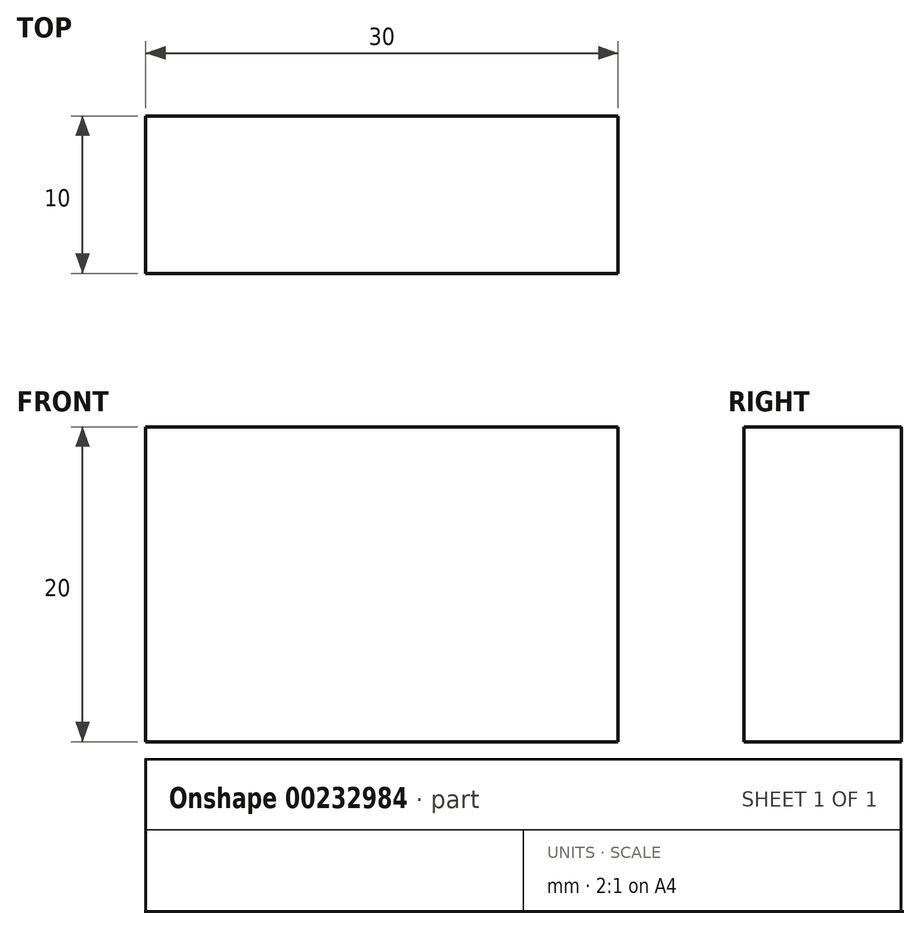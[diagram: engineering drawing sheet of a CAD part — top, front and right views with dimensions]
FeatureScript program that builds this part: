
annotation { "Feature Type Name" : "Feature", "Feature Type Description" : "" }
export const myFeature = defineFeature(function(context is Context, id is Id, definition is map)
    precondition{}
    {
        {
            var Q0;
            Q0=qCreatedBy(makeId("Front.planeOp"),FACE);
            var sketch = newSketch(context, id + "F0", { "sketchPlane" : qUnion([Q0])});
            skLineSegment(sketch, "E0.bottom", {"start": v(0, 0) * mm, "end": v(30, 0) * mm});
            skLineSegment(sketch, "E0.top", {"start": v(0, 20) * mm, "end": v(30, 20) * mm});
            skLineSegment(sketch, "E0.left", {"start": v(0, 0) * mm, "end": v(0, 20) * mm});
            skLineSegment(sketch, "E0.right", {"start": v(30, 0) * mm, "end": v(30, 20) * mm});
            skSolve(sketch);
        }
        {
            var Q0;
            Q0 = qSketchRegion(id + "F0", true);
            extrude(context, id + "F1", {"entities" : qUnion([Q0]), "depth" : 10 * mm});
        }
    });
